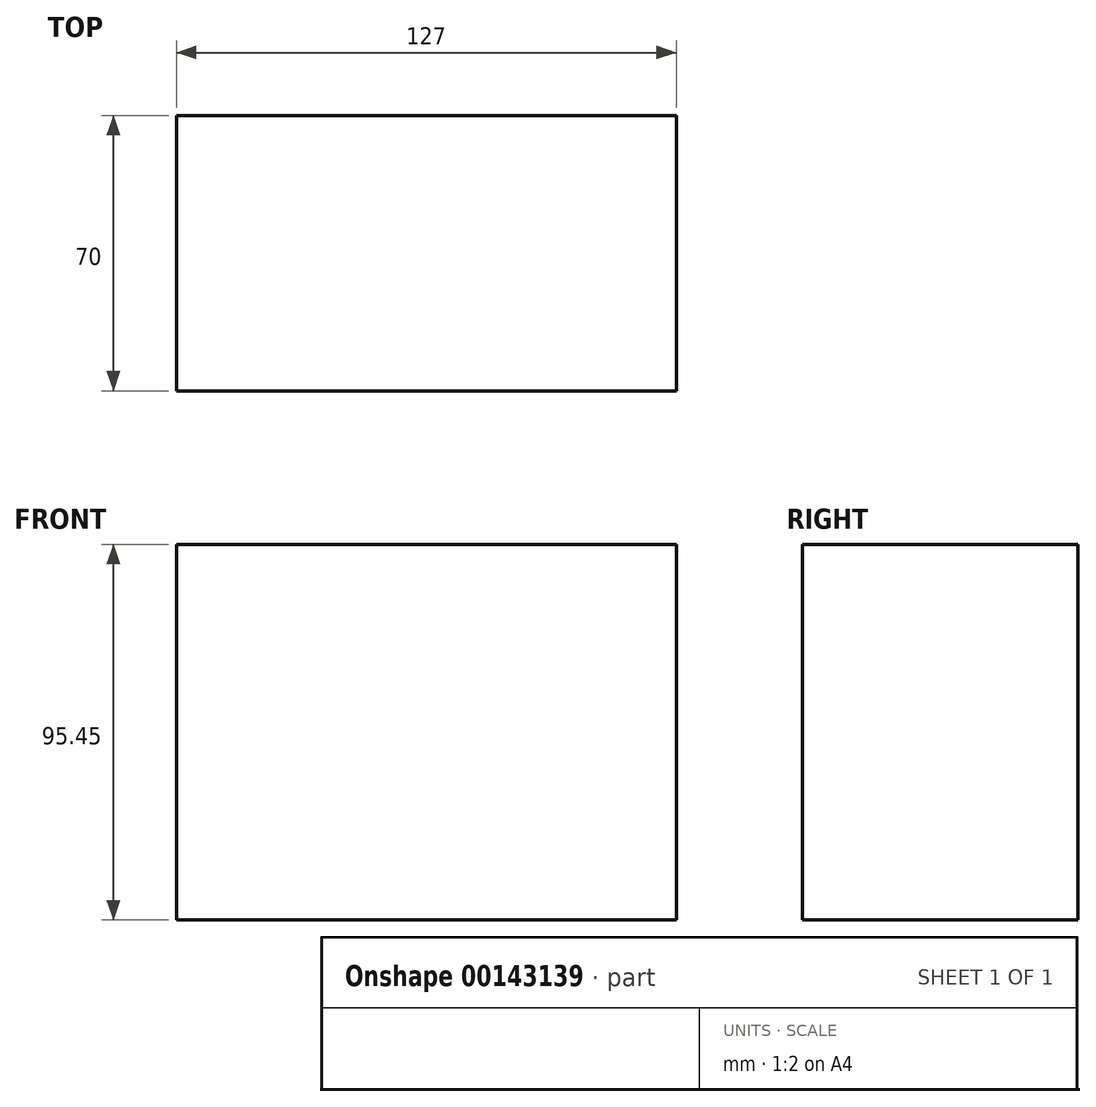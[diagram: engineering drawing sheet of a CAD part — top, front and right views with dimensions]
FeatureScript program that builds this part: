
annotation { "Feature Type Name" : "Feature", "Feature Type Description" : "" }
export const myFeature = defineFeature(function(context is Context, id is Id, definition is map)
    precondition{}
    {
        {
            var Q0;
            Q0=qCreatedBy(makeId("Front.planeOp"),FACE);
            var sketch = newSketch(context, id + "F0", { "sketchPlane" : qUnion([Q0])});
            skLineSegment(sketch, "E0.bottom", {"start": v(-59.8, 31.73) * mm, "end": v(67.2, 31.73) * mm});
            skLineSegment(sketch, "E0.top", {"start": v(-59.8, -63.72) * mm, "end": v(67.2, -63.72) * mm});
            skLineSegment(sketch, "E0.left", {"start": v(-59.8, 31.73) * mm, "end": v(-59.8, -63.72) * mm});
            skLineSegment(sketch, "E0.right", {"start": v(67.2, 31.73) * mm, "end": v(67.2, -63.72) * mm});
            skSolve(sketch);
        }
        {
            var Q0;
            Q0 = qSketchRegion(id + "F0", true);
            extrude(context, id + "F1", {"entities" : qUnion([Q0]), "depth" : 70 * mm});
        }
    });
